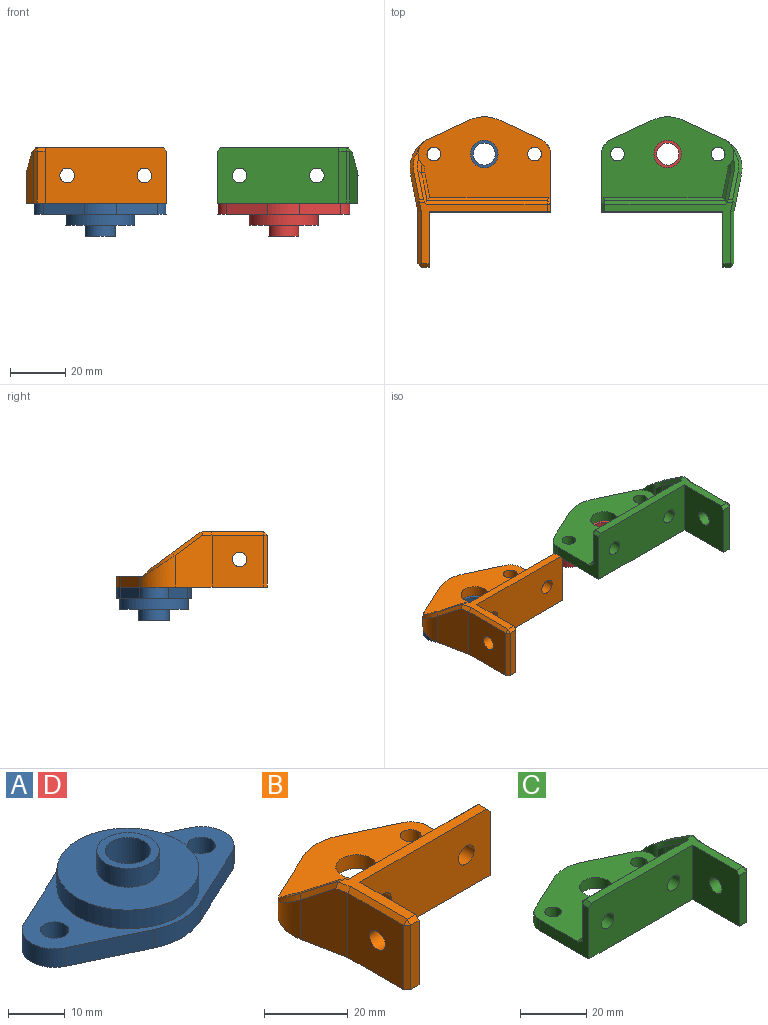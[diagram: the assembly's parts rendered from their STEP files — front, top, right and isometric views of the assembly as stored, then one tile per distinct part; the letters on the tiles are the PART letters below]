
ASSEMBLY  parts=4 mates=3
PART A: 17 faces, bbox 48x27x12 mm
  f0: cylinder r=5.75mm len=10.41mm, axis (0,0,-1), area 52.1mm2, adj f1,f9,f11,f12
  f1: plane 14.96x7.02mm, normal (-0.42,-0.91,0), area 66.1mm2, adj f0,f2,f11,f12
  f2: cylinder r=13.5mm len=11.47mm, axis (0,0,-1), area 47.4mm2, adj f1,f3,f11,f12
  f3: plane 14.96x7.02mm, normal (0.42,-0.91,0), area 66.1mm2, adj f2,f4,f11,f12
  f4: cylinder r=5.75mm len=10.41mm, axis (0,0,-1), area 52.1mm2, adj f3,f5,f11,f12
  f5: plane 14.96x7.02mm, normal (0.42,0.91,0), area 66.1mm2, adj f4,f6,f11,f12
  f6: cylinder r=13.5mm len=11.47mm, axis (0,0,-1), area 47.4mm2, adj f5,f9,f11,f12
  f7: cylinder r=2.5mm len=5mm, axis (0,0,-1), area 62.8mm2, adj f11,f12
  f8: cylinder r=4mm len=12mm, axis (0,0,-1), area 301.6mm2, adj f12,f16
  f9: plane 14.96x7.02mm, normal (-0.42,0.91,0), area 66.1mm2, adj f0,f6,f11,f12
  f10: cylinder r=2.5mm len=5mm, axis (0,0,-1), area 62.8mm2, adj f11,f12
  f11: plane 48x27mm, normal (0,0,1), area 340.7mm2, adj f0,f1,f2,f3,f4,f5,f6,f7
  f12: plane 48x27mm, normal (0,0,-1), area 781.3mm2, adj f0,f1,f2,f3,f4,f5,f6,f7
  f13: cylinder r=12.5mm len=25mm, axis (0,0,-1), area 314.2mm2, adj f11,f14
  f14: plane 25x25mm, normal (0,0,1), area 395.8mm2, adj f13,f15
  f15: cylinder r=5.5mm len=11mm, axis (0,0,-1), area 138.2mm2, adj f14,f16
  f16: plane 11x11mm, normal (0,0,1), area 44.8mm2, adj f8,f15
PART B: 44 faces, bbox 51.2x54.5x20 mm
  f0: plane 48x30mm, normal (0,0,1), area 1037.6mm2, adj f1,f8,f9,f10,f11,f12,f13,f14
  f1: cylinder r=5.75mm len=4mm, axis (0,0,1), area 3.5mm2, adj f0,f2,f14,f16,f31
  f2: cylinder r=12mm len=12.48mm, axis (0,0,1), area 106.3mm2, adj f1,f3,f16,f31
  f3: plane 18.8x13.37mm, normal (-0.98,-0.2,0), area 219mm2, adj f2,f4,f16,f30,f32
  f4: plane 18.8x18.8mm, normal (-1,0,0), area 331.4mm2, adj f3,f16,f25,f26,f29
  f5: plane 18.8x2.83mm, normal (0,-1,0), area 53.2mm2, adj f6,f16,f26,f27
  f6: plane 20x20mm, normal (1,0,0), area 377.2mm2, adj f5,f7,f16,f20,f25,f27
  f7: plane 43.97x20mm, normal (0,-1,0), area 834.5mm2, adj f6,f8,f16,f20,f23,f24,f34
  f8: plane 21x18.8mm, normal (1,0,0), area 126.5mm2, adj f0,f7,f9,f16,f34,f36,f40
  f9: cylinder r=5.75mm len=5.21mm, axis (0,0,1), area 26mm2, adj f0,f8,f10,f16
  f10: plane 14.96x7.02mm, normal (0.42,0.91,0), area 66.1mm2, adj f0,f9,f11,f16
  f11: cylinder r=13.5mm len=11.47mm, axis (0,0,1), area 47.4mm2, adj f0,f10,f14,f16
  f12: cylinder r=2.5mm len=5mm, axis (0,0,1), area 62.8mm2, adj f0,f16
  f13: cylinder r=5mm len=10mm, axis (0,0,1), area 125.7mm2, adj f0,f16
  f14: plane 14.96x7.02mm, normal (-0.42,0.91,0), area 66.1mm2, adj f0,f1,f11,f16
  f15: cylinder r=2.5mm len=5mm, axis (0,0,1), area 62.8mm2, adj f0,f16
  f16: plane 54.5x50.9mm, normal (0,0,-1), area 1446.6mm2, adj f1,f2,f3,f4,f5,f6,f7,f8
  f17: cylinder r=5.75mm len=8.53mm, axis (0,0,-1), area 25.9mm2, adj f0,f18,f22,f31,f39,f43
  f18: cylinder r=8mm len=5.89mm, axis (0,0,-1), area 14.7mm2, adj f17,f19,f39,f43
  f19: plane 13.32x10.16mm, normal (0.98,0.2,0), area 99.5mm2, adj f18,f21,f38,f42
  f20: plane 46.29x22.36mm, normal (0,0,1), area 183.2mm2, adj f6,f7,f27,f29,f30,f33,f34,f37
  f21: plane 43.75x13.6mm, normal (0,1,0), area 547.8mm2, adj f19,f23,f24,f33,f36,f38,f41
  f22: plane 18.26x13.38mm, normal (0,0.59,0.81), area 30.5mm2, adj f17,f31,f32,f37,f38,f39
  f23: cylinder r=2.65mm len=5.3mm, axis (0,-1,0), area 66.6mm2, adj f7,f21
  f24: cylinder r=2.65mm len=5.3mm, axis (0,-1,0), area 66.6mm2, adj f7,f21
  f25: cylinder r=2.65mm len=5.3mm, axis (-1,0,0), area 67.1mm2, adj f4,f6
  f26: plane 18.8x1.2mm, normal (-0.71,-0.71,0), area 31.9mm2, adj f4,f5,f16,f28
  f27: plane 2.83x1.2mm, normal (0,-0.71,0.71), area 4.8mm2, adj f5,f6,f20,f28
  f28: plane 1.2x1.2mm, normal (-0.58,-0.58,0.58), area 1.2mm2, adj f26,f27,f29
  f29: plane 18.92x1.2mm, normal (-0.71,0,0.71), area 32mm2, adj f4,f20,f28,f30
  f30: plane 3.75x1.87mm, normal (-0.69,-0.14,0.71), area 6.1mm2, adj f3,f20,f29,f32,f37
  f31: bspline ~12.85x9.44mm, area 20.3mm2, adj f1,f2,f17,f22,f32
  f32: plane 10.94x8.46mm, normal (-0.74,0.3,0.61), area 23mm2, adj f3,f22,f30,f31,f37
  f33: plane 43.77x1.2mm, normal (0,0.71,0.71), area 74.3mm2, adj f20,f21,f35,f38
  f34: plane 2.8x1.2mm, normal (0.71,0,0.71), area 4.8mm2, adj f7,f8,f20,f35
  f35: plane 1.2x1.2mm, normal (0.58,0.58,0.58), area 1.2mm2, adj f33,f34,f36
  f36: plane 13.6x1.2mm, normal (0.71,0.71,0), area 23.1mm2, adj f8,f21,f35,f40
  f37: plane 2x0.8mm, normal (0,0.31,0.95), area 1.5mm2, adj f20,f22,f30,f32,f38
  f38: plane 11.89x8.91mm, normal (0.66,0.53,0.54), area 24.5mm2, adj f19,f20,f21,f22,f33,f37,f39
  f39: bspline ~5.28x4.56mm, area 9.8mm2, adj f17,f18,f22,f38
  f40: plane 2.4x1.2mm, normal (0.5,0.5,0.71), area 2.3mm2, adj f0,f8,f36,f41
  f41: plane 44.02x1.2mm, normal (0,0.71,0.71), area 73.4mm2, adj f0,f21,f40,f42
  f42: plane 10.39x3.01mm, normal (0.69,0.14,0.71), area 16.7mm2, adj f0,f19,f41,f43
  f43: cone r=6.8mm half-angle=45deg, axis (0,0,1), area 4.4mm2, adj f0,f17,f18,f42
PART C: 44 faces, bbox 51.2x54.5x20 mm
  f0: plane 48x30mm, normal (0,0,1), area 1037.6mm2, adj f1,f8,f9,f10,f11,f12,f13,f14
  f1: cylinder r=5.75mm len=4mm, axis (0,0,1), area 3.5mm2, adj f0,f2,f14,f16,f31
  f2: cylinder r=12mm len=12.48mm, axis (0,0,1), area 106.3mm2, adj f1,f3,f16,f31
  f3: plane 18.8x13.37mm, normal (0.98,-0.2,0), area 219mm2, adj f2,f4,f16,f30,f32
  f4: plane 18.8x18.8mm, normal (1,0,0), area 331.4mm2, adj f3,f16,f25,f26,f29
  f5: plane 18.8x2.83mm, normal (0,-1,0), area 53.2mm2, adj f6,f16,f26,f27
  f6: plane 20x20mm, normal (-1,0,0), area 377.2mm2, adj f5,f7,f16,f20,f25,f27
  f7: plane 43.97x20mm, normal (0,-1,0), area 834.5mm2, adj f6,f8,f16,f20,f23,f24,f34
  f8: plane 21x18.8mm, normal (-1,0,0), area 126.5mm2, adj f0,f7,f9,f16,f34,f36,f40
  f9: cylinder r=5.75mm len=5.21mm, axis (0,0,1), area 26mm2, adj f0,f8,f10,f16
  f10: plane 14.96x7.02mm, normal (-0.42,0.91,0), area 66.1mm2, adj f0,f9,f11,f16
  f11: cylinder r=13.5mm len=11.47mm, axis (0,0,1), area 47.4mm2, adj f0,f10,f14,f16
  f12: cylinder r=2.5mm len=5mm, axis (0,0,1), area 62.8mm2, adj f0,f16
  f13: cylinder r=5mm len=10mm, axis (0,0,1), area 125.7mm2, adj f0,f16
  f14: plane 14.96x7.02mm, normal (0.42,0.91,0), area 66.1mm2, adj f0,f1,f11,f16
  f15: cylinder r=2.5mm len=5mm, axis (0,0,1), area 62.8mm2, adj f0,f16
  f16: plane 54.5x50.9mm, normal (0,0,-1), area 1446.6mm2, adj f1,f2,f3,f4,f5,f6,f7,f8
  f17: cylinder r=5.75mm len=8.53mm, axis (0,0,-1), area 25.9mm2, adj f0,f18,f22,f31,f39,f43
  f18: cylinder r=8mm len=5.89mm, axis (0,0,-1), area 14.7mm2, adj f17,f19,f39,f43
  f19: plane 13.32x10.16mm, normal (-0.98,0.2,0), area 99.5mm2, adj f18,f21,f38,f42
  f20: plane 46.29x22.36mm, normal (0,0,1), area 183.2mm2, adj f6,f7,f27,f29,f30,f33,f34,f37
  f21: plane 43.75x13.6mm, normal (0,1,0), area 547.8mm2, adj f19,f23,f24,f33,f36,f38,f41
  f22: plane 18.26x13.38mm, normal (0,0.59,0.81), area 30.5mm2, adj f17,f31,f32,f37,f38,f39
  f23: cylinder r=2.65mm len=5.3mm, axis (0,-1,0), area 66.6mm2, adj f7,f21
  f24: cylinder r=2.65mm len=5.3mm, axis (0,-1,0), area 66.6mm2, adj f7,f21
  f25: cylinder r=2.65mm len=5.3mm, axis (1,0,0), area 67.1mm2, adj f4,f6
  f26: plane 18.8x1.2mm, normal (0.71,-0.71,0), area 31.9mm2, adj f4,f5,f16,f28
  f27: plane 2.83x1.2mm, normal (0,-0.71,0.71), area 4.8mm2, adj f5,f6,f20,f28
  f28: plane 1.2x1.2mm, normal (0.58,-0.58,0.58), area 1.2mm2, adj f26,f27,f29
  f29: plane 18.92x1.2mm, normal (0.71,0,0.71), area 32mm2, adj f4,f20,f28,f30
  f30: plane 3.75x1.87mm, normal (0.69,-0.14,0.71), area 6.1mm2, adj f3,f20,f29,f32,f37
  f31: bspline ~12.85x9.44mm, area 20.3mm2, adj f1,f2,f17,f22,f32
  f32: plane 10.94x8.46mm, normal (0.74,0.3,0.61), area 23mm2, adj f3,f22,f30,f31,f37
  f33: plane 43.77x1.2mm, normal (0,0.71,0.71), area 74.3mm2, adj f20,f21,f35,f38
  f34: plane 2.8x1.2mm, normal (-0.71,0,0.71), area 4.8mm2, adj f7,f8,f20,f35
  f35: plane 1.2x1.2mm, normal (-0.58,0.58,0.58), area 1.2mm2, adj f33,f34,f36
  f36: plane 13.6x1.2mm, normal (-0.71,0.71,0), area 23.1mm2, adj f8,f21,f35,f40
  f37: plane 2x0.8mm, normal (0,0.31,0.95), area 1.5mm2, adj f20,f22,f30,f32,f38
  f38: plane 11.89x8.91mm, normal (-0.66,0.53,0.54), area 24.5mm2, adj f19,f20,f21,f22,f33,f37,f39
  f39: bspline ~5.51x4.73mm, area 9.8mm2, adj f17,f18,f22,f38
  f40: plane 2.4x1.2mm, normal (-0.5,0.5,0.71), area 2.3mm2, adj f0,f8,f36,f41
  f41: plane 44.02x1.2mm, normal (0,0.71,0.71), area 73.4mm2, adj f0,f21,f40,f42
  f42: plane 10.39x3.01mm, normal (-0.69,0.14,0.71), area 16.7mm2, adj f0,f19,f41,f43
  f43: cone r=6.8mm half-angle=45deg, axis (0,0,1), area 4.4mm2, adj f0,f17,f18,f42
PART D: same geometry as A
PLACE A rot(axis=(1,0,0),180deg) t=(-33.25,0,0)mm
PLACE B t=(24.75,0,4)mm
PLACE C t=(33.25,0,4)mm
PLACE D rot(axis=(1,0,0),180deg) t=(33.25,0,0)mm
MATE revolute B.f12 <-> A.f7  axis (0,0,1) through (-51.5,0,0)mm
MATE revolute D.f7 <-> C.f15  axis (0,0,1) through (15,0,0)mm
MATE planar C.f16 <-> B.f16  axis (0,0,-1) through (35.17,-7.68,0)mm
